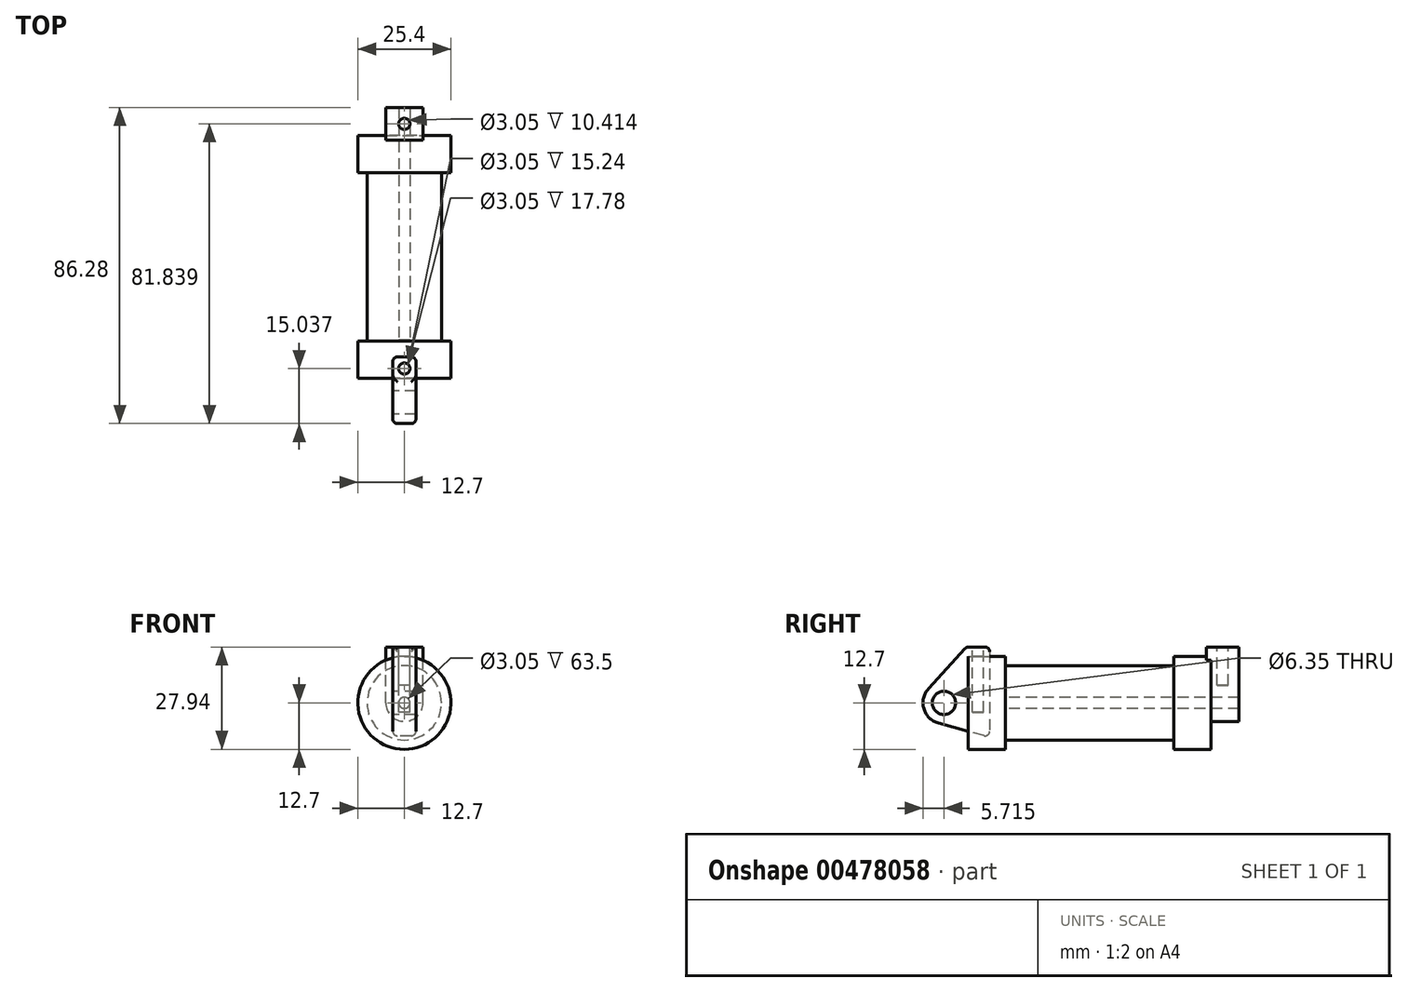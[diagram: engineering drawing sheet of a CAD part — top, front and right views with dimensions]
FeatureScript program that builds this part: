
annotation { "Feature Type Name" : "Feature", "Feature Type Description" : "" }
export const myFeature = defineFeature(function(context is Context, id is Id, definition is map)
    precondition{}
    {
        {
            var Q0;
            Q0=qCreatedBy(makeId("Right.planeOp"),FACE);
            var sketch = newSketch(context, id + "F0", { "sketchPlane" : qUnion([Q0])});
            skLineSegment(sketch, "E0", {"start": v(0, 0) * mm, "end": v(0, 12.7) * mm});
            skLineSegment(sketch, "E1", {"start": v(0, 12.7) * mm, "end": v(10.16, 12.7) * mm});
            skLineSegment(sketch, "E2", {"start": v(10.16, 12.7) * mm, "end": v(10.16, 10.16) * mm});
            skLineSegment(sketch, "E3", {"start": v(10.16, 10.16) * mm, "end": v(56.13, 10.16) * mm});
            skLineSegment(sketch, "E4", {"start": v(56.13, 10.16) * mm, "end": v(56.13, 12.7) * mm});
            skLineSegment(sketch, "E5", {"start": v(56.13, 12.7) * mm, "end": v(66.3, 12.7) * mm});
            skLineSegment(sketch, "E6", {"start": v(66.3, 12.7) * mm, "end": v(66.3, 0) * mm});
            skLineSegment(sketch, "E7", {"start": v(66.3, 0) * mm, "end": v(0, 0) * mm});
            skLineSegment(sketch, "E8", {"start": v(5.84, 15.24) * mm, "end": v(-0.5, 15.24) * mm});
            skLineSegment(sketch, "E9", {"start": v(-0.5, 15.24) * mm, "end": v(-10.88, 3.85) * mm});
            skLineSegment(sketch, "E10", {"start": v(0, 0) * mm, "end": v(-6.65, 0) * mm});
            skCircle(sketch, "E11", {"center": v(-6.65, 0) * mm, "radius": 5.72 * mm});
            skCircle(sketch, "E12", {"center": v(-6.65, 0) * mm, "radius": 3.18 * mm});
            skLineSegment(sketch, "E13", {"start": v(5.84, 15.24) * mm, "end": v(5.84, -9.4) * mm});
            skLineSegment(sketch, "E14", {"start": v(5.84, -9.4) * mm, "end": v(-8.18, -5.5) * mm});
            skSolve(sketch);
        }
        {
            var Q0;
            {var subQ0=sQuery(id+"F0.wireOp",EDGE,"E14");Q0=makeQuery(id+"F0.imprint","IMPRINT",FACE,{"disambiguationData":[TD([[makeQuery(id+"F0.imprint","IMPRINT",EDGE,{"derivedFrom":subQ0}),-1.0]])]});}
            var Q1;
            {var subQ5=sQuery(id+"F0.wireOp",EDGE,"E12");Q1=makeQuery(id+"F0.imprint","IMPRINT",FACE,{"disambiguationData":[TD([[makeQuery(id+"F0.imprint","IMPRINT",EDGE,{"derivedFrom":subQ5}),-1.0]])]});}
            var Q2;
            {var subQ1=sQuery(id+"F0.wireOp",EDGE,"E0");Q2=makeQuery(id+"F0.imprint","IMPRINT",FACE,{"disambiguationData":[TD([[makeQuery(id+"F0.imprint","IMPRINT",EDGE,{"derivedFrom":subQ1}),1.0]])]});}
            var Q3;
            {var subQ0=sQuery(id+"F0.wireOp",EDGE,"E0");Q3=makeQuery(id+"F0.imprint","IMPRINT",FACE,{"disambiguationData":[TD([[makeQuery(id+"F0.imprint","IMPRINT",EDGE,{"derivedFrom":subQ0}),-1.0]])]});}
            extrude(context, id + "F1", {"entities" : qUnion([Q0, Q1, Q2, Q3]), "depth" : 3.17 * mm, "hasSecondDirection" : true, "secondDirectionOppositeDirection" : true, "secondDirectionDepth" : 3.17 * mm});
        }
        {
            var Q0;
            {var subQ0=sQuery(id+"F0.wireOp",EDGE,"E2");Q0=makeQuery(id+"F0.imprint","IMPRINT",FACE,{"disambiguationData":[TD([[makeQuery(id+"F0.imprint","IMPRINT",EDGE,{"derivedFrom":subQ0}),-1.0]])]});}
            var Q1;
            {var subQ0=sQuery(id+"F0.wireOp",EDGE,"E0");Q1=makeQuery(id+"F0.imprint","IMPRINT",FACE,{"disambiguationData":[TD([[makeQuery(id+"F0.imprint","IMPRINT",EDGE,{"derivedFrom":subQ0}),-1.0]])]});}
            var Q2;
            Q2=sQuery(id+"F0.wireOp",EDGE,"E7");
            revolve(context, id + "F2", {"entities" : qUnion([Q0, Q1]), "axis" : qUnion([Q2]), "revolveType" : RevolveType.FULL});
        }
        {
            var Q0;
            Q0=makeQuery(id+"F2.opRevolve","SWEPT_FACE",FACE,{"disambiguationData":[OSD([sQuery(id+"F0.wireOp",EDGE,"E6")])]});
            var sketch = newSketch(context, id + "F3", { "sketchPlane" : qUnion([Q0])});
            skCircle(sketch, "E15", {"center": v(0, 0) * mm, "radius": 1.52 * mm});
            skCircle(sketch, "E16", {"center": v(0, 0) * mm, "radius": 5.06 * mm});
            skLineSegment(sketch, "E17", {"start": v(-5.06, 0) * mm, "end": v(-5.06, 15.24) * mm});
            skLineSegment(sketch, "E18", {"start": v(5.06, 0) * mm, "end": v(5.06, 15.24) * mm});
            skLineSegment(sketch, "E19", {"start": v(-5.06, 15.24) * mm, "end": v(5.06, 15.24) * mm});
            skSolve(sketch);
        }
        {
            var Q0;
            Q0 = qSketchRegion(id + "F3", true);
            extrude(context, id + "F4", {"entities" : qUnion([Q0]), "operationType" : NewBodyOperationType.ADD, "depth" : 7.62 * mm, "hasSecondDirection" : true, "secondDirectionOppositeDirection" : true, "secondDirectionDepth" : 1.27 * mm});
        }
        {
            var Q0;
            Q0=makeQuery(id+"F4.boolean.opBoolean","SPLIT",FACE,{"disambiguationData":[TD([makeQuery(id+"F4.opExtrude","SWEPT_FACE",FACE,{"disambiguationData":[OSD([sQuery(id+"F3.wireOp",EDGE,"E15")])]})])],"derivedFrom":makeQuery(id+"F2.opRevolve","SWEPT_FACE",FACE,{"disambiguationData":[OSD([sQuery(id+"F0.wireOp",EDGE,"E6")])]})});
            extrude(context, id + "F5", {"entities" : qUnion([Q0]), "operationType" : NewBodyOperationType.REMOVE, "oppositeDirection" : true, "depth" : 55.88 * mm});
        }
        {
            var Q0;
            Q0=makeQuery(id+"F4.opExtrude","SWEPT_FACE",FACE,{"disambiguationData":[OSD([sQuery(id+"F3.wireOp",EDGE,"E19")])]});
            var sketch = newSketch(context, id + "F6", { "sketchPlane" : qUnion([Q0])});
            skCircle(sketch, "E20", {"center": v(0, 69.47) * mm, "radius": 1.52 * mm});
            skSolve(sketch);
        }
        {
            var Q0;
            Q0=makeQuery(id+"F1.opExtrude","SWEPT_FACE",FACE,{"disambiguationData":[OSD([sQuery(id+"F0.wireOp",EDGE,"E8")])]});
            var sketch = newSketch(context, id + "F7", { "sketchPlane" : qUnion([Q0])});
            skCircle(sketch, "E21", {"center": v(0, 2.67) * mm, "radius": 1.52 * mm});
            skSolve(sketch);
        }
        {
            var Q0;
            Q0 = qSketchRegion(id + "F6", true);
            extrude(context, id + "F8", {"entities" : qUnion([Q0]), "operationType" : NewBodyOperationType.REMOVE, "oppositeDirection" : true, "depth" : 10.4 * mm});
        }
        {
            var Q0;
            Q0 = qSketchRegion(id + "F7", true);
            extrude(context, id + "F9", {"entities" : qUnion([Q0]), "operationType" : NewBodyOperationType.REMOVE, "oppositeDirection" : true, "depth" : 17.78 * mm});
        }
        {
            var Q0;
            Q0=makeQuery(id+"F2.opRevolve","SWEPT_FACE",FACE,{"disambiguationData":[OSD([sQuery(id+"F0.wireOp",EDGE,"E2")])]});
            var Q1;
            Q1=makeQuery(id+"F2.opRevolve","SWEPT_FACE",FACE,{"disambiguationData":[OSD([sQuery(id+"F0.wireOp",EDGE,"E4")])]});
            var Q2;
            Q2=makeQuery(id+"F2.opRevolve","SWEPT_FACE",FACE,{"disambiguationData":[OSD([sQuery(id+"F0.wireOp",EDGE,"E5")])]});
            var Q3;
            Q3=makeQuery(id+"F2.opRevolve","SWEPT_FACE",FACE,{"disambiguationData":[OSD([sQuery(id+"F0.wireOp",EDGE,"E1")])]});
            var Q4;
            Q4=makeQuery(id+"F4.opExtrude","CAP_FACE",FACE,{"disambiguationData":[OSD([sQuery(id+"F3.wireOp",EDGE,"E15"),sQuery(id+"F3.wireOp",EDGE,"E16"),sQuery(id+"F3.wireOp",EDGE,"E17"),sQuery(id+"F3.wireOp",EDGE,"E18"),sQuery(id+"F3.wireOp",EDGE,"E19")])],"isStart":true});
            var Q5;
            Q5=makeQuery(id+"F1.opExtrude","SWEPT_FACE",FACE,{"disambiguationData":[OSD([sQuery(id+"F0.wireOp",EDGE,"E13")])]});
            var Q6;
            Q6=makeQuery(id+"F4.opExtrude","SWEPT_FACE",FACE,{"disambiguationData":[OSD([sQuery(id+"F3.wireOp",EDGE,"E18")])]});
            var Q7;
            Q7=makeQuery(id+"F4.opExtrude","SWEPT_FACE",FACE,{"disambiguationData":[OSD([sQuery(id+"F3.wireOp",EDGE,"E17")])]});
            var Q8;
            Q8=makeQuery(id+"F1.opExtrude","SWEPT_FACE",FACE,{"disambiguationData":[OSD([sQuery(id+"F0.wireOp",EDGE,"E9")])]});
            var Q9;
            Q9=makeQuery(id+"F2.opRevolve","SWEPT_FACE",FACE,{"disambiguationData":[OSD([sQuery(id+"F0.wireOp",EDGE,"E3")])]});
            fillet(context, id + "F10", {"entities" : qUnion([Q0, Q1, Q2, Q3, Q4, Q5, Q6, Q7, Q8, Q9]), "radius" : 1.27 * mm, "tangentPropagation" : true, "allowEdgeOverflow" : false});
        }
    });
